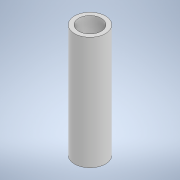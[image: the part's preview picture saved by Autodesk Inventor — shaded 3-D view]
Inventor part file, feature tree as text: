
AUTODESK INVENTOR PART (.ipt)
format: ipt  version: 2020.3 (Build 243373000, 373)  size: 97,792 bytes
history: native  units: mm
features: extrude x1, sketch x1
ambient origin geometry x8: Origin, YZ Plane, XZ Plane, XY Plane, X Axis, Y Axis, Z Axis, Center Point
bodies: Solid1 (feature_tree)
feature tree (2):
  extrude  "Extrusion1"  Depth=10.0mm
  sketch  "Sketch1"  dims[d0=13.6mm d1=10.0mm d2=50.0mm d3=0.0mm]
